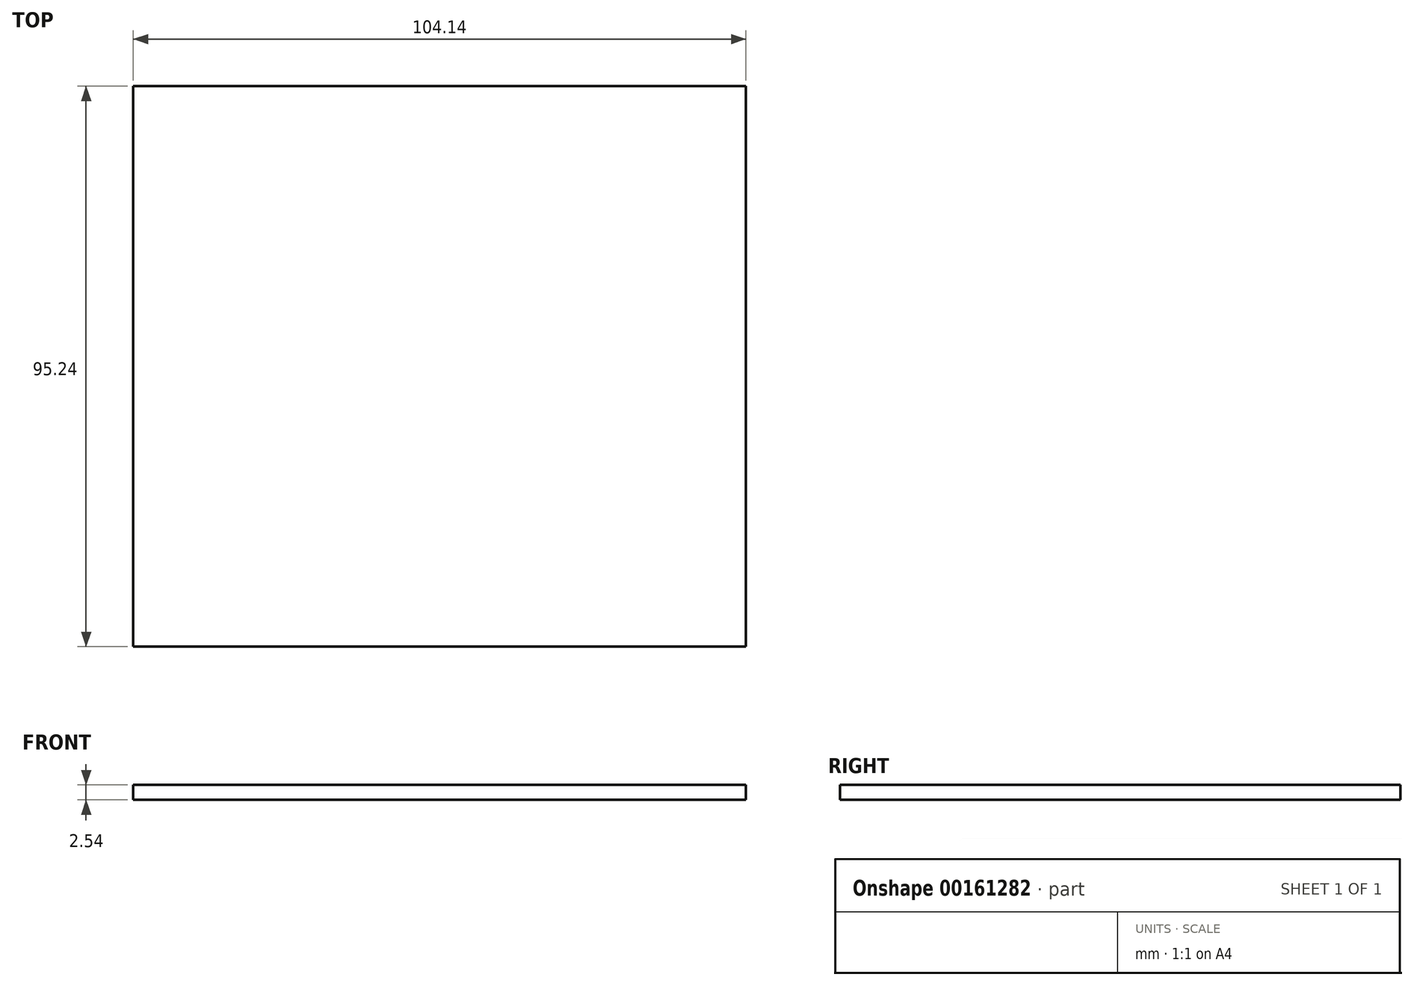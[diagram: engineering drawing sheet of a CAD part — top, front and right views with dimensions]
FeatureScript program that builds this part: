
annotation { "Feature Type Name" : "Feature", "Feature Type Description" : "" }
export const myFeature = defineFeature(function(context is Context, id is Id, definition is map)
    precondition{}
    {
        {
            var Q0;
            Q0=qCreatedBy(makeId("Top.planeOp"),FACE);
            var sketch = newSketch(context, id + "F0", { "sketchPlane" : qUnion([Q0])});
            skLineSegment(sketch, "E0.bottom", {"start": v(52.07, 47.62) * mm, "end": v(-52.07, 47.62) * mm});
            skLineSegment(sketch, "E0.top", {"start": v(52.07, -47.63) * mm, "end": v(-52.07, -47.63) * mm});
            skLineSegment(sketch, "E0.left", {"start": v(52.07, 47.63) * mm, "end": v(52.07, -47.62) * mm});
            skLineSegment(sketch, "E0.right", {"start": v(-52.07, 47.62) * mm, "end": v(-52.07, -47.63) * mm});
            skPoint(sketch, "E0.middle", {"position": v(0, 0) * mm});
            skSolve(sketch);
        }
        {
            var Q0;
            Q0=makeQuery(id+"F0.imprint","IMPRINT",FACE,{"disambiguationData":[TD([[makeQuery(id+"F0.imprint","IMPRINT",EDGE,{"derivedFrom":sQuery(id+"F0.wireOp",EDGE,"E0.bottom")}),1.0]])]});
            extrude(context, id + "F1", {"entities" : qUnion([Q0]), "depth" : 2.54 * mm});
        }
    });
